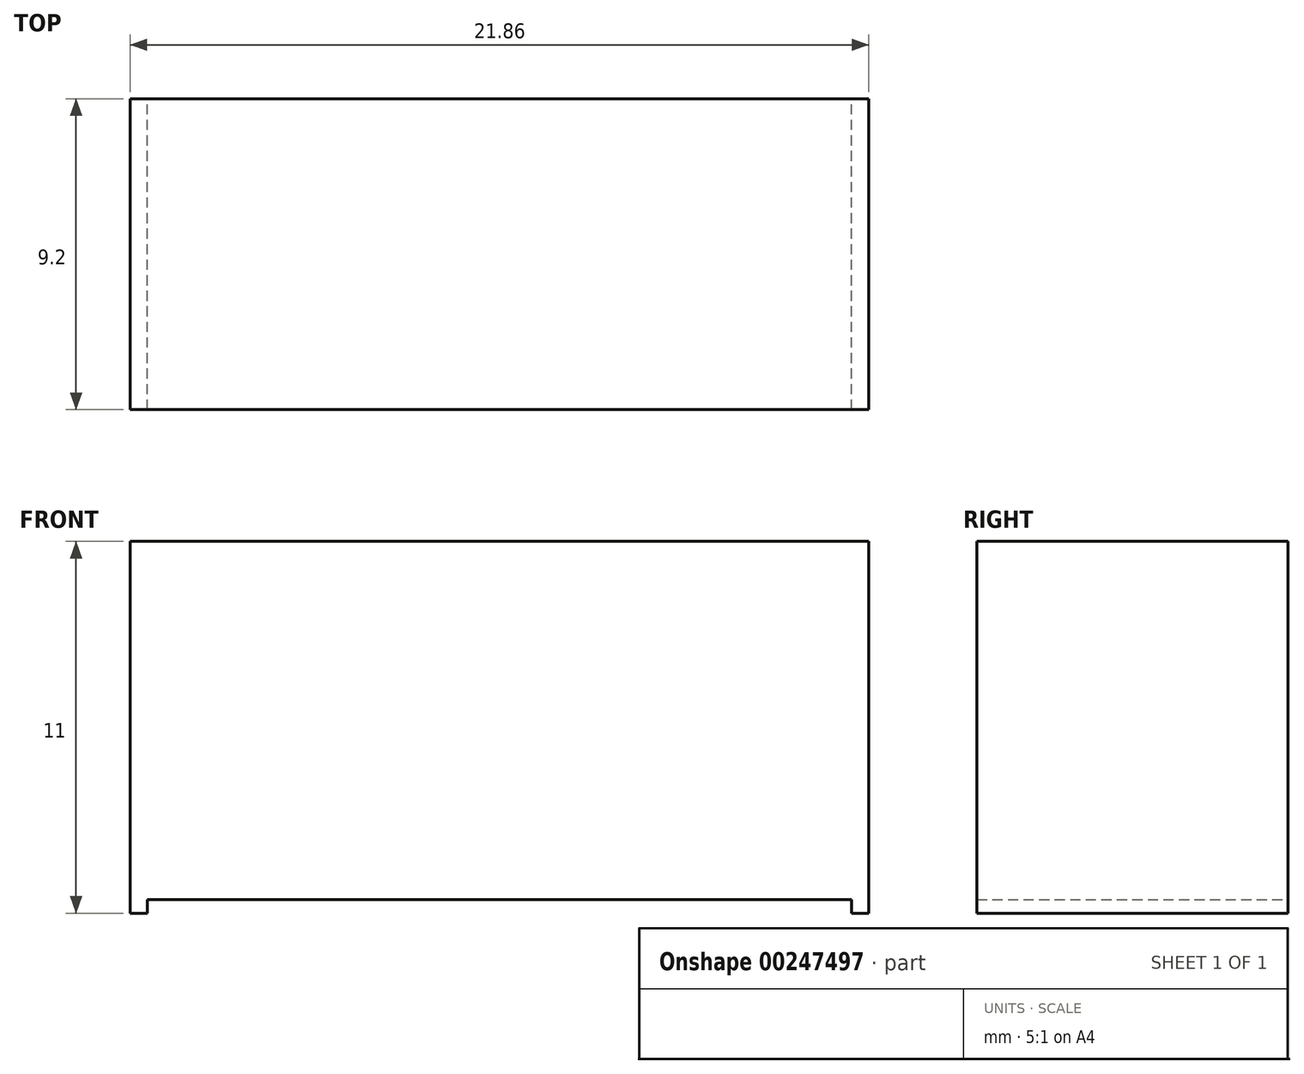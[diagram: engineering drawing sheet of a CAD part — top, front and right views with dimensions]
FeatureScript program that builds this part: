
annotation { "Feature Type Name" : "Feature", "Feature Type Description" : "" }
export const myFeature = defineFeature(function(context is Context, id is Id, definition is map)
    precondition{}
    {
        {
            var Q0;
            Q0=qCreatedBy(makeId("Top.planeOp"),FACE);
            var sketch = newSketch(context, id + "F0", { "sketchPlane" : qUnion([Q0])});
            skLineSegment(sketch, "E0.bottom", {"start": v(10.93, -4.6) * mm, "end": v(-10.93, -4.6) * mm});
            skLineSegment(sketch, "E0.top", {"start": v(10.93, 4.6) * mm, "end": v(-10.93, 4.6) * mm});
            skLineSegment(sketch, "E0.left", {"start": v(10.93, -4.6) * mm, "end": v(10.93, 4.6) * mm});
            skLineSegment(sketch, "E0.right", {"start": v(-10.93, -4.6) * mm, "end": v(-10.93, 4.6) * mm});
            skPoint(sketch, "E0.middle", {"position": v(0, 0) * mm});
            skSolve(sketch);
        }
        {
            var Q0;
            Q0=qSketchRegion(id+"F0",true);
            extrude(context, id + "F1", {"entities" : qUnion([Q0]), "depth" : 10.6 * mm});
        }
        {
            var Q0;
            Q0=makeQuery(id+"F1.opExtrude","CAP_FACE",FACE,{"disambiguationData":[OSD([sQuery(id+"F0.wireOp",EDGE,"E0.bottom"),sQuery(id+"F0.wireOp",EDGE,"E0.top"),sQuery(id+"F0.wireOp",EDGE,"E0.left"),sQuery(id+"F0.wireOp",EDGE,"E0.right")])],"isStart":true});
            var sketch = newSketch(context, id + "F2", { "sketchPlane" : qUnion([Q0])});
            skLineSegment(sketch, "E1.bottom", {"start": v(-10.93, 4.6) * mm, "end": v(-10.43, 4.6) * mm});
            skLineSegment(sketch, "E1.top", {"start": v(-10.93, -4.6) * mm, "end": v(-10.43, -4.6) * mm});
            skLineSegment(sketch, "E1.left", {"start": v(-10.93, 4.6) * mm, "end": v(-10.93, -4.6) * mm});
            skLineSegment(sketch, "E1.right", {"start": v(-10.43, 4.6) * mm, "end": v(-10.43, -4.6) * mm});
            skLineSegment(sketch, "E2", {"start": v(0, 4.6) * mm, "end": v(0, -4.6) * mm, "construction": true});
            skLineSegment(sketch, "E3.MirrorCS", {"start": v(10.93, -4.6) * mm, "end": v(10.43, -4.6) * mm});
            skLineSegment(sketch, "E4.MirrorCS", {"start": v(10.93, 4.6) * mm, "end": v(10.43, 4.6) * mm});
            skLineSegment(sketch, "E5.MirrorCS", {"start": v(10.43, 4.6) * mm, "end": v(10.43, -4.6) * mm});
            skLineSegment(sketch, "E6.MirrorCS", {"start": v(10.93, 4.6) * mm, "end": v(10.93, -4.6) * mm});
            skSolve(sketch);
        }
        {
            var Q0;
            Q0=qSketchRegion(id+"F2",true);
            extrude(context, id + "F3", {"entities" : qUnion([Q0]), "operationType" : NewBodyOperationType.ADD, "depth" : .4 * mm});
        }
    });
